# Revit family: Tub_Filler-DXV-Modulus-D35120981_Series
name_source: partatom
category: Plumbing Fixtures
units: mm (PartAtom-declared; Revit-internal decimal feet)

## family parameters
Cut with Voids When Loaded = No
Host = Face
OmniClass Number = 23.45.05.14.21
OmniClass Title = Bathtubs
Part Type = Normal
Room Calculation Point = No
Round Connector Dimension = Use Diameter
Shared = Yes

## types (4) — shared parameters
ASME A112.18.1/CSA B125.1 = Yes
ASSE 1016 = Yes
Assembly Code = D2020300
CEC Compliant = Yes
CW Connection = Yes
CWFU = 3
CalGreen Compliant = Yes
Cold Water Connection Diameter = 1/2"
D35000981.191 Wall Mount Tub Filler Rough Valve = No
Default Elevation = 40"
Description = DXV Modulus Wall Mount Tub Filler
EPA WaterSense® Certified = Yes
Flow Rate = 1.8 gpm (6.8 L/min)
HW Connection = Yes
HWFU = 3
Height = 3 3/4"
Hot Water Connection Diameter = 1/2"
Installation Instruction Link = https://dxv01.blob.core.windows.net
Installation Type = Wall Mount
Length = 15 3/4"
Manufacturer = DXV
Price = Prices may vary. Please consult Manufacturer Representative for most up-to-date price list.
Product Documentation Link = https://dxv01.blob.core.windows.net
Product Page URL = https://www.dxv.com
Revised Date = 04/06/2022
Rough Valve Option = Yes
URL = https://www.dxv.com
Vent Connection = No
WFU = 4
Wall Mount Tub Filler Option = Yes
Waste Connection = No
Water Connection Diameter = 1/2"
Width = 8 15/16"

## per-type parameters (varying)
| type | Finish | Material |
| D35120981.100 | Brass-DXV-100-Polished Chrome | Brass-DXV-100-Polished Chrome |
| D35120981.144 | Brass-DXV-144-Brushed Nickel | Brass-DXV-144-Brushed Nickel |
| D35120981.150 | Brass-DXV-150-Platinum Nickel | Brass-DXV-150-Platinum Nickel |
| D35120981.243 | Brass-DXV-243-Matte Black | Brass-DXV-243-Matte Black |

note: column(s) folded — value = type name in every type: Model

## geometry (parser evidence)
native form markers: Sweep x2
no freeform markers — native parametric forms only
